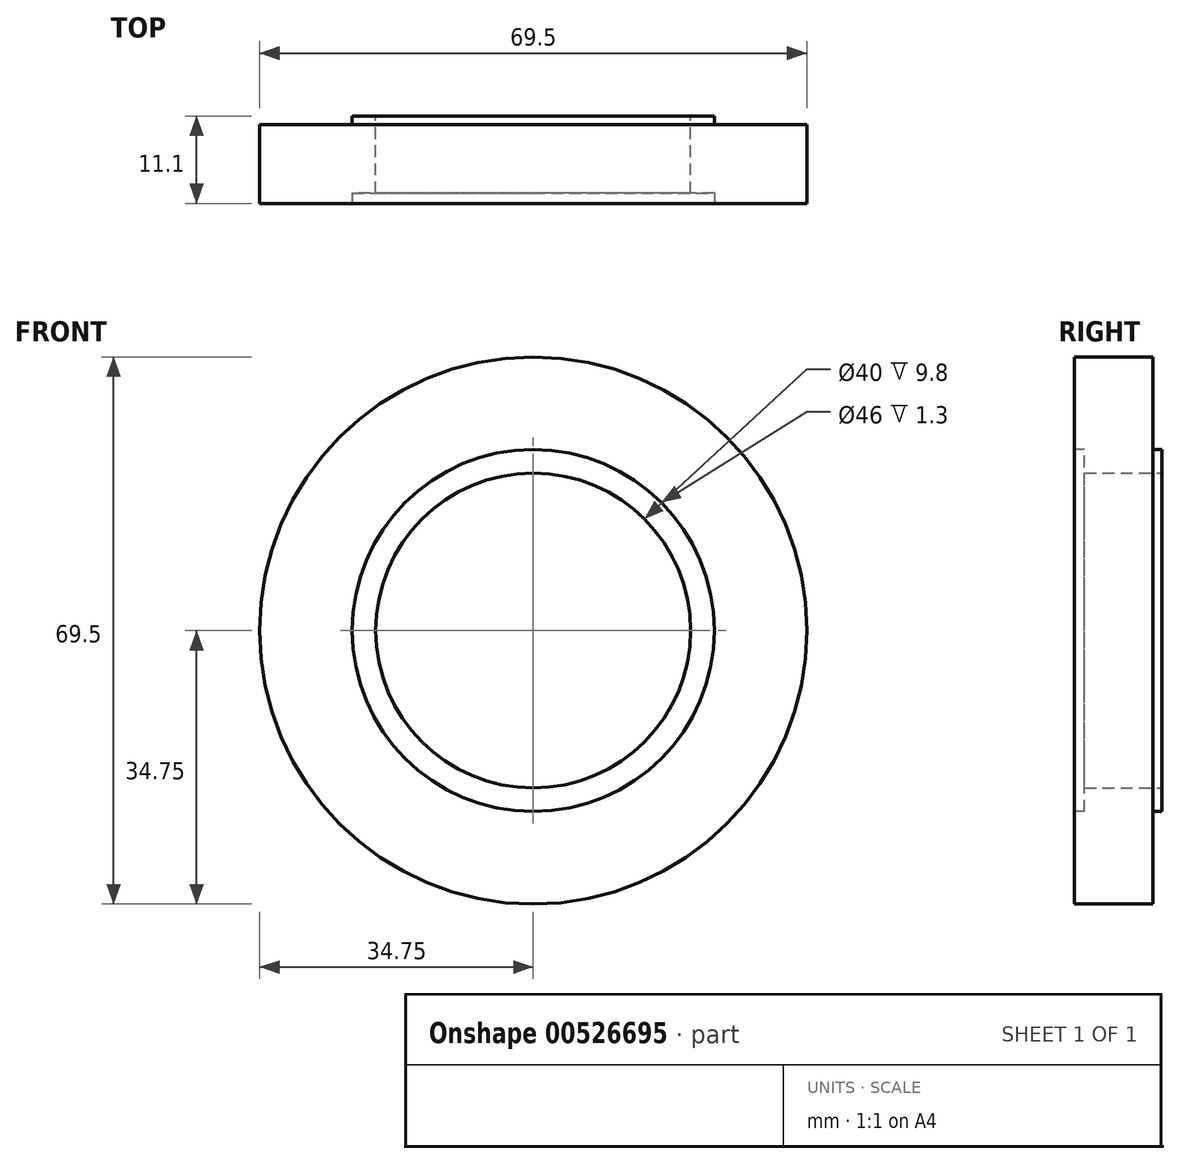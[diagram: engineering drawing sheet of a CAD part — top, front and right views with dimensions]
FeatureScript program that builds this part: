
annotation { "Feature Type Name" : "Feature", "Feature Type Description" : "" }
export const myFeature = defineFeature(function(context is Context, id is Id, definition is map)
    precondition{}
    {
        {
            var Q0;
            Q0=qCreatedBy(makeId("Front.planeOp"),FACE);
            var sketch = newSketch(context, id + "F0", { "sketchPlane" : qUnion([Q0])});
            skCircle(sketch, "E0", {"center": v(0, 0) * mm, "radius": 34.75 * mm});
            skCircle(sketch, "E1", {"center": v(0, 0) * mm, "radius": 20 * mm});
            skSolve(sketch);
        }
        {
            var Q0;
            Q0 = qSketchRegion(id + "F0", true);
            extrude(context, id + "F1", {"entities" : qUnion([Q0]), "depth" : 10 * mm, "offsetDistance" : 25 * mm});
        }
        {
            var Q0;
            Q0=makeQuery(id+"F1.opExtrude","CAP_FACE",FACE,{"disambiguationData":[OSD([sQuery(id+"F0.wireOp",EDGE,"E0"),sQuery(id+"F0.wireOp",EDGE,"E1")])],"isStart":false});
            var sketch = newSketch(context, id + "F2", { "sketchPlane" : qUnion([Q0])});
            skCircle(sketch, "E2", {"center": v(0, 0) * mm, "radius": 23 * mm});
            skSolve(sketch);
        }
        {
            var Q0;
            Q0=makeQuery(id+"F2.imprint","IMPRINT",FACE,{"disambiguationData":[TD([[makeQuery(id+"F2.imprint","IMPRINT",EDGE,{"derivedFrom":sQuery(id+"F2.wireOp",EDGE,"E2")}),1.0]])]});
            extrude(context, id + "F3", {"entities" : qUnion([Q0]), "operationType" : NewBodyOperationType.REMOVE, "oppositeDirection" : true, "depth" : 1.3 * mm, "offsetDistance" : 25 * mm});
        }
        {
            var Q0;
            Q0=makeQuery(id+"F1.opExtrude","CAP_FACE",FACE,{"disambiguationData":[OSD([sQuery(id+"F0.wireOp",EDGE,"E0"),sQuery(id+"F0.wireOp",EDGE,"E1")])],"isStart":true});
            var sketch = newSketch(context, id + "F4", { "sketchPlane" : qUnion([Q0])});
            skCircle(sketch, "E3", {"center": v(0, 0) * mm, "radius": 23 * mm});
            skSolve(sketch);
        }
        {
            var Q0;
            Q0=makeQuery(id+"F4.imprint","IMPRINT",FACE,{"disambiguationData":[TD([[makeQuery(id+"F4.imprint","IMPRINT",EDGE,{"derivedFrom":sQuery(id+"F4.wireOp",EDGE,"E3")}),1.0]])]});
            extrude(context, id + "F5", {"entities" : qUnion([Q0]), "operationType" : NewBodyOperationType.ADD, "depth" : 1.1 * mm, "offsetDistance" : 25 * mm});
        }
    });
